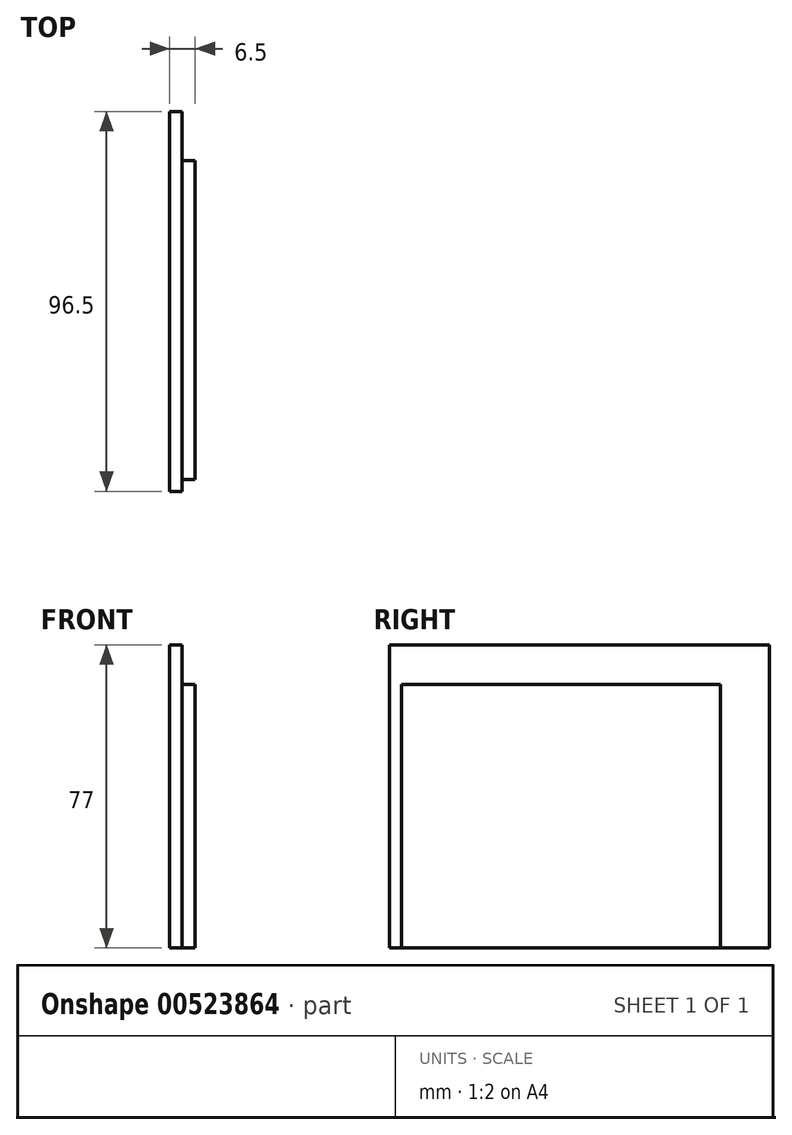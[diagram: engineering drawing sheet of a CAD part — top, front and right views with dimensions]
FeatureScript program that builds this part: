
annotation { "Feature Type Name" : "Feature", "Feature Type Description" : "" }
export const myFeature = defineFeature(function(context is Context, id is Id, definition is map)
    precondition{}
    {
        {
            var Q0;
            Q0=qCreatedBy(makeId("Right.planeOp"),FACE);
            var sketch = newSketch(context, id + "F0", { "sketchPlane" : qUnion([Q0])});
            skLineSegment(sketch, "E0.bottom", {"start": v(-48.25, 38.5) * mm, "end": v(48.25, 38.5) * mm});
            skLineSegment(sketch, "E0.top", {"start": v(-48.25, -38.5) * mm, "end": v(48.25, -38.5) * mm});
            skLineSegment(sketch, "E0.left", {"start": v(-48.25, 38.5) * mm, "end": v(-48.25, -38.5) * mm});
            skLineSegment(sketch, "E0.right", {"start": v(48.25, 38.5) * mm, "end": v(48.25, -38.5) * mm});
            skPoint(sketch, "E0.middle", {"position": v(0, 0) * mm});
            skSolve(sketch);
        }
        {
            var Q0;
            Q0 = qSketchRegion(id + "F0", true);
            extrude(context, id + "F1", {"entities" : qUnion([Q0]), "endBound" : BoundingType.SYMMETRIC, "depth" : 3.2 * mm, "offsetDistance" : 25 * mm});
        }
        {
            var Q0;
            Q0=makeQuery(id+"F1.opExtrude","CAP_FACE",FACE,{"disambiguationData":[OSD([sQuery(id+"F0.wireOp",EDGE,"E0.bottom"),sQuery(id+"F0.wireOp",EDGE,"E0.top"),sQuery(id+"F0.wireOp",EDGE,"E0.left"),sQuery(id+"F0.wireOp",EDGE,"E0.right")])],"isStart":false});
            var sketch = newSketch(context, id + "F2", { "sketchPlane" : qUnion([Q0])});
            skLineSegment(sketch, "E1.bottom", {"start": v(-45.25, 28.5) * mm, "end": v(35.75, 28.5) * mm});
            skLineSegment(sketch, "E1.top", {"start": v(-45.25, -38.5) * mm, "end": v(35.75, -38.5) * mm});
            skLineSegment(sketch, "E1.left", {"start": v(-45.25, 28.5) * mm, "end": v(-45.25, -38.5) * mm});
            skLineSegment(sketch, "E1.right", {"start": v(35.75, 28.5) * mm, "end": v(35.75, -38.5) * mm});
            skSolve(sketch);
        }
        {
            var Q0;
            Q0=makeQuery(id+"F2.imprint","IMPRINT",FACE,{"disambiguationData":[TD([[makeQuery(id+"F2.imprint","IMPRINT",EDGE,{"derivedFrom":sQuery(id+"F2.wireOp",EDGE,"E1.bottom")}),-1.0]])]});
            extrude(context, id + "F3", {"entities" : qUnion([Q0]), "operationType" : NewBodyOperationType.ADD, "depth" : 3.3 * mm, "offsetDistance" : 25 * mm});
        }
    });
